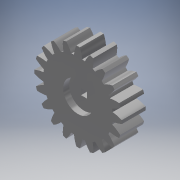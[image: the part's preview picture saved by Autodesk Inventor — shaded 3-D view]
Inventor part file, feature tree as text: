
AUTODESK INVENTOR PART (.ipt)
format: ipt  version: 2019 (Build 230136000, 136)  size: 288,768 bytes
history: native  units: mm (DEFAULTED — no unit token found)
features: sketch x4, extrude x3, plane x3, other x3
ambient origin geometry x8: Origin, YZ Plane, XZ Plane, XY Plane, X Axis, Y Axis, Z Axis, Center Point
bodies: Solid1 (feature_tree)
feature tree (13):
  extrude  "Extrusion1"  Depth=12.0mm TaperAngle=0.0deg
  plane  "Work Plane2"
  plane  "Work Plane8"
  plane  "Work Plane9"
  other  "Spur Gear"
  extrude  "Extrusion2"  Depth=10.0mm TaperAngle=0.0deg
  extrude  "Extrusion3"  Depth=1.570796mm TaperAngle=0.0deg
  sketch  "Sketch1"  dims[d0=44.0mm d1=12.0mm d2=0.0mm]
  sketch  "Sketch2"  dims[d3=40.0mm d4=10.0mm d5=0.0mm]
  other  "Srf1"
  sketch  "Sketch5"  dims[d16=40.0mm d17=0.0mm d34=1.570796mm]
  sketch  "Sketch6"  dims[d39=0.0mm d41=0.0mm d43=40.0mm d46=40.0mm d47=0.0mm d48=0.0mm d49=3.0mm d50=3.0mm d51=12.0mm d52=0.0mm d53=15.0mm d54=3.0mm d55=0.0mm]
  other  "Pitch Diameter"
